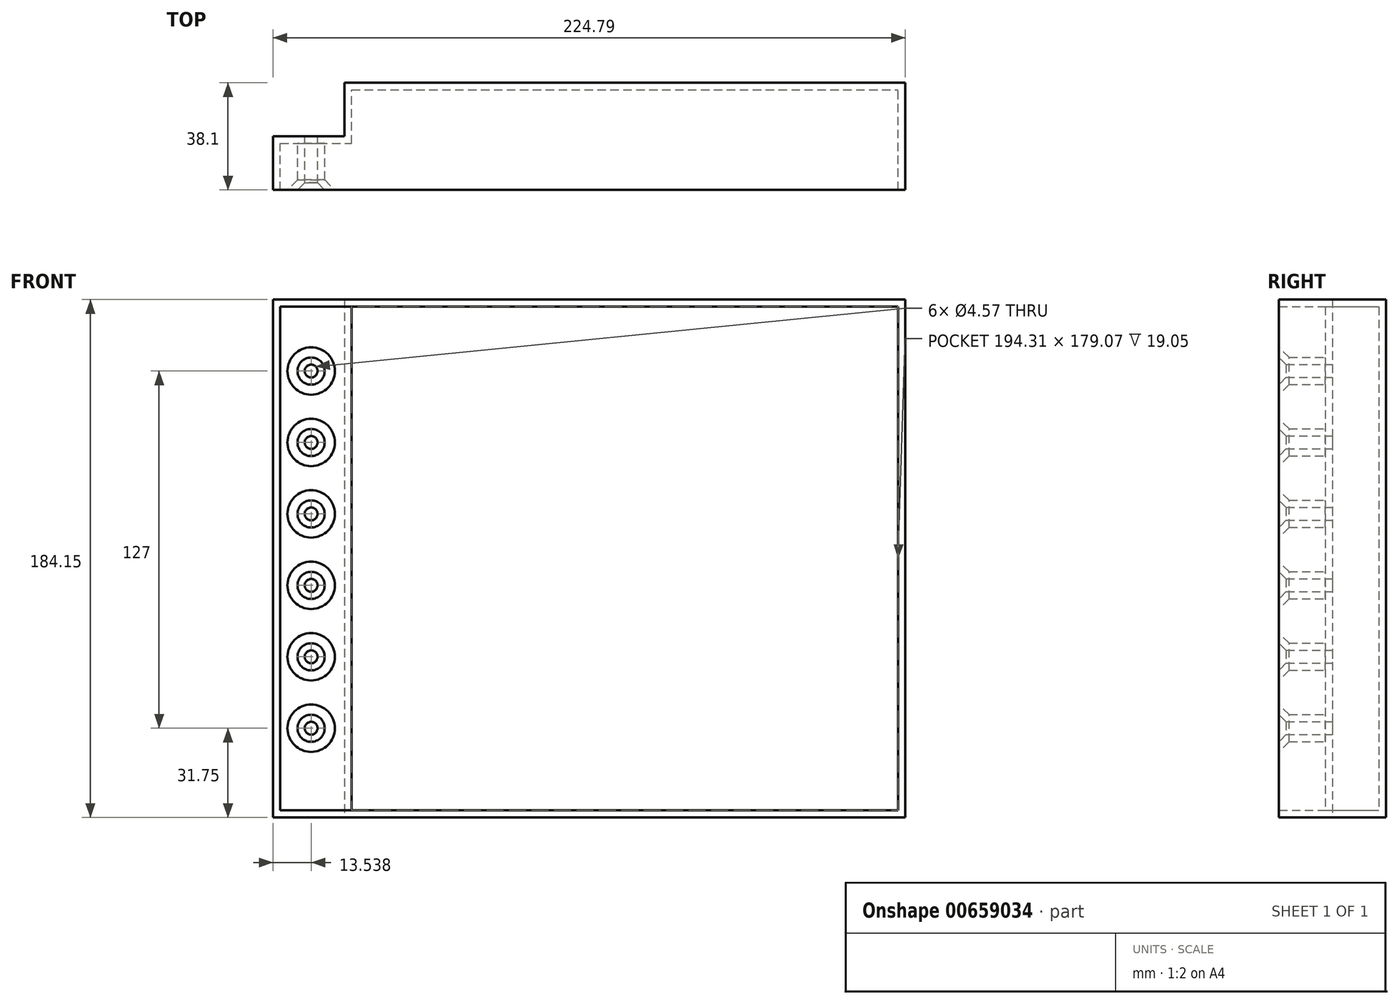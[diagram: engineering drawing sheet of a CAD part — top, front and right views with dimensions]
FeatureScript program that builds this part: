
annotation { "Feature Type Name" : "Feature", "Feature Type Description" : "" }
export const myFeature = defineFeature(function(context is Context, id is Id, definition is map)
    precondition{}
    {
        {
            var Q0;
            Q0=qCreatedBy(makeId("Top.planeOp"),FACE);
            var sketch = newSketch(context, id + "F0", { "sketchPlane" : qUnion([Q0])});
            skLineSegment(sketch, "E0.bottom", {"start": v(0, 0) * mm, "end": v(199.4, 0) * mm});
            skLineSegment(sketch, "E0.top", {"start": v(0, 38.1) * mm, "end": v(199.4, 38.1) * mm});
            skLineSegment(sketch, "E0.left", {"start": v(0, 0) * mm, "end": v(0, 38.1) * mm});
            skLineSegment(sketch, "E0.right", {"start": v(199.4, 0) * mm, "end": v(199.4, 38.1) * mm});
            skSolve(sketch);
        }
        {
            var Q0;
            Q0=makeQuery(id+"F0.imprint","IMPRINT",FACE,{"disambiguationData":[TD([[makeQuery(id+"F0.imprint","IMPRINT",EDGE,{"derivedFrom":sQuery(id+"F0.wireOp",EDGE,"E0.bottom")}),1.0]])]});
            extrude(context, id + "F1", {"entities" : qUnion([Q0]), "depth" : 184.15 * mm, "offsetDistance" : 25.4 * mm});
        }
        {
            var Q0;
            Q0=makeQuery(id+"F1.opExtrude","SWEPT_FACE",FACE,{"disambiguationData":[OSD([sQuery(id+"F0.wireOp",EDGE,"E0.left")])]});
            var sketch = newSketch(context, id + "F2", { "sketchPlane" : qUnion([Q0])});
            skLineSegment(sketch, "E1.bottom", {"start": v(0, 184.15) * mm, "end": v(-19.05, 184.15) * mm});
            skLineSegment(sketch, "E1.top", {"start": v(0, 0) * mm, "end": v(-19.05, 0) * mm});
            skLineSegment(sketch, "E1.left", {"start": v(0, 184.15) * mm, "end": v(0, 0) * mm});
            skLineSegment(sketch, "E1.right", {"start": v(-19.05, 184.15) * mm, "end": v(-19.05, 0) * mm});
            skSolve(sketch);
        }
        {
            var Q0;
            Q0=makeQuery(id+"F2.imprint","IMPRINT",FACE,{"disambiguationData":[TD([[makeQuery(id+"F2.imprint","IMPRINT",EDGE,{"derivedFrom":sQuery(id+"F2.wireOp",EDGE,"E1.bottom")}),1.0]])]});
            extrude(context, id + "F3", {"entities" : qUnion([Q0]), "operationType" : NewBodyOperationType.ADD, "depth" : 25.4 * mm, "offsetDistance" : 25.4 * mm});
        }
        {
            var Q0;
            Q0=makeQuery(id+"F3.opExtrude","SWEPT_FACE",FACE,{"disambiguationData":[OSD([sQuery(id+"F2.wireOp",EDGE,"E1.right")])]});
            var sketch = newSketch(context, id + "F4", { "sketchPlane" : qUnion([Q0])});
            skCircle(sketch, "E2", {"center": v(11.86, 158.75) * mm, "radius": 2.29 * mm});
            skCircle(sketch, "E3.0.1.0", {"center": v(11.86, 133.35) * mm, "radius": 2.29 * mm});
            skCircle(sketch, "E3.0.2.0", {"center": v(11.86, 107.95) * mm, "radius": 2.29 * mm});
            skCircle(sketch, "E3.0.3.0", {"center": v(11.86, 82.55) * mm, "radius": 2.29 * mm});
            skCircle(sketch, "E3.0.4.0", {"center": v(11.86, 57.15) * mm, "radius": 2.29 * mm});
            skCircle(sketch, "E3.0.5.0", {"center": v(11.86, 31.75) * mm, "radius": 2.29 * mm});
            skLineSegment(sketch, "E3.direction1", {"start": v(11.86, 158.75) * mm, "end": v(38.1, 158.75) * mm, "construction": true});
            skLineSegment(sketch, "E3.direction2", {"start": v(11.86, 158.75) * mm, "end": v(11.86, 133.35) * mm, "construction": true});
            skSolve(sketch);
        }
        {
            var Q0;
            Q0 = qSketchRegion(id + "F4", true);
            extrude(context, id + "F5", {"entities" : qUnion([Q0]), "operationType" : NewBodyOperationType.REMOVE, "oppositeDirection" : true, "depth" : 25.4 * mm, "offsetDistance" : 25.4 * mm});
        }
        {
            var Q0;
            Q0=makeQuery(id+"F5.boolean.opBoolean","INTERSECT",EDGE,{"derivedFrom":[makeQuery(id+"F3.boolean.opBoolean","MERGE",FACE,{"derivedFrom":[makeQuery(id+"F1.opExtrude","SWEPT_FACE",FACE,{"disambiguationData":[OSD([sQuery(id+"F0.wireOp",EDGE,"E0.bottom")])]}),makeQuery(id+"F3.opExtrude","SWEPT_FACE",FACE,{"disambiguationData":[OSD([sQuery(id+"F2.wireOp",EDGE,"E1.left")])]})]}),makeQuery(id+"F5.opExtrude","SWEPT_FACE",FACE,{"disambiguationData":[OSD([sQuery(id+"F4.wireOp",EDGE,"E2")])]})]});
            var Q1;
            Q1=makeQuery(id+"F5.boolean.opBoolean","INTERSECT",EDGE,{"derivedFrom":[makeQuery(id+"F3.boolean.opBoolean","MERGE",FACE,{"derivedFrom":[makeQuery(id+"F1.opExtrude","SWEPT_FACE",FACE,{"disambiguationData":[OSD([sQuery(id+"F0.wireOp",EDGE,"E0.bottom")])]}),makeQuery(id+"F3.opExtrude","SWEPT_FACE",FACE,{"disambiguationData":[OSD([sQuery(id+"F2.wireOp",EDGE,"E1.left")])]})]}),makeQuery(id+"F5.opExtrude","SWEPT_FACE",FACE,{"disambiguationData":[OSD([sQuery(id+"F4.wireOp",EDGE,"E3.0.1.0")])]})]});
            var Q2;
            Q2=makeQuery(id+"F5.boolean.opBoolean","INTERSECT",EDGE,{"derivedFrom":[makeQuery(id+"F3.boolean.opBoolean","MERGE",FACE,{"derivedFrom":[makeQuery(id+"F1.opExtrude","SWEPT_FACE",FACE,{"disambiguationData":[OSD([sQuery(id+"F0.wireOp",EDGE,"E0.bottom")])]}),makeQuery(id+"F3.opExtrude","SWEPT_FACE",FACE,{"disambiguationData":[OSD([sQuery(id+"F2.wireOp",EDGE,"E1.left")])]})]}),makeQuery(id+"F5.opExtrude","SWEPT_FACE",FACE,{"disambiguationData":[OSD([sQuery(id+"F4.wireOp",EDGE,"E3.0.2.0")])]})]});
            var Q3;
            Q3=makeQuery(id+"F5.boolean.opBoolean","INTERSECT",EDGE,{"derivedFrom":[makeQuery(id+"F3.boolean.opBoolean","MERGE",FACE,{"derivedFrom":[makeQuery(id+"F1.opExtrude","SWEPT_FACE",FACE,{"disambiguationData":[OSD([sQuery(id+"F0.wireOp",EDGE,"E0.bottom")])]}),makeQuery(id+"F3.opExtrude","SWEPT_FACE",FACE,{"disambiguationData":[OSD([sQuery(id+"F2.wireOp",EDGE,"E1.left")])]})]}),makeQuery(id+"F5.opExtrude","SWEPT_FACE",FACE,{"disambiguationData":[OSD([sQuery(id+"F4.wireOp",EDGE,"E3.0.3.0")])]})]});
            var Q4;
            Q4=makeQuery(id+"F5.boolean.opBoolean","INTERSECT",EDGE,{"derivedFrom":[makeQuery(id+"F3.boolean.opBoolean","MERGE",FACE,{"derivedFrom":[makeQuery(id+"F1.opExtrude","SWEPT_FACE",FACE,{"disambiguationData":[OSD([sQuery(id+"F0.wireOp",EDGE,"E0.bottom")])]}),makeQuery(id+"F3.opExtrude","SWEPT_FACE",FACE,{"disambiguationData":[OSD([sQuery(id+"F2.wireOp",EDGE,"E1.left")])]})]}),makeQuery(id+"F5.opExtrude","SWEPT_FACE",FACE,{"disambiguationData":[OSD([sQuery(id+"F4.wireOp",EDGE,"E3.0.4.0")])]})]});
            var Q5;
            Q5=makeQuery(id+"F5.boolean.opBoolean","INTERSECT",EDGE,{"derivedFrom":[makeQuery(id+"F3.boolean.opBoolean","MERGE",FACE,{"derivedFrom":[makeQuery(id+"F1.opExtrude","SWEPT_FACE",FACE,{"disambiguationData":[OSD([sQuery(id+"F0.wireOp",EDGE,"E0.bottom")])]}),makeQuery(id+"F3.opExtrude","SWEPT_FACE",FACE,{"disambiguationData":[OSD([sQuery(id+"F2.wireOp",EDGE,"E1.left")])]})]}),makeQuery(id+"F5.opExtrude","SWEPT_FACE",FACE,{"disambiguationData":[OSD([sQuery(id+"F4.wireOp",EDGE,"E3.0.5.0")])]})]});
            chamfer(context, id + "F6", {"entities" : qUnion([Q0, Q1, Q2, Q3, Q4, Q5]), "width" : 2.54 * mm, "tangentPropagation" : true});
        }
        {
            var Q0;
            Q0=makeQuery(id+"F3.boolean.opBoolean","MERGE",FACE,{"derivedFrom":[makeQuery(id+"F1.opExtrude","SWEPT_FACE",FACE,{"disambiguationData":[OSD([sQuery(id+"F0.wireOp",EDGE,"E0.bottom")])]}),makeQuery(id+"F3.opExtrude","SWEPT_FACE",FACE,{"disambiguationData":[OSD([sQuery(id+"F2.wireOp",EDGE,"E1.left")])]})]});
            shell(context, id + "F7", {"entities" : qUnion([Q0]), "thickness" : 2.54 * mm});
        }
    });
